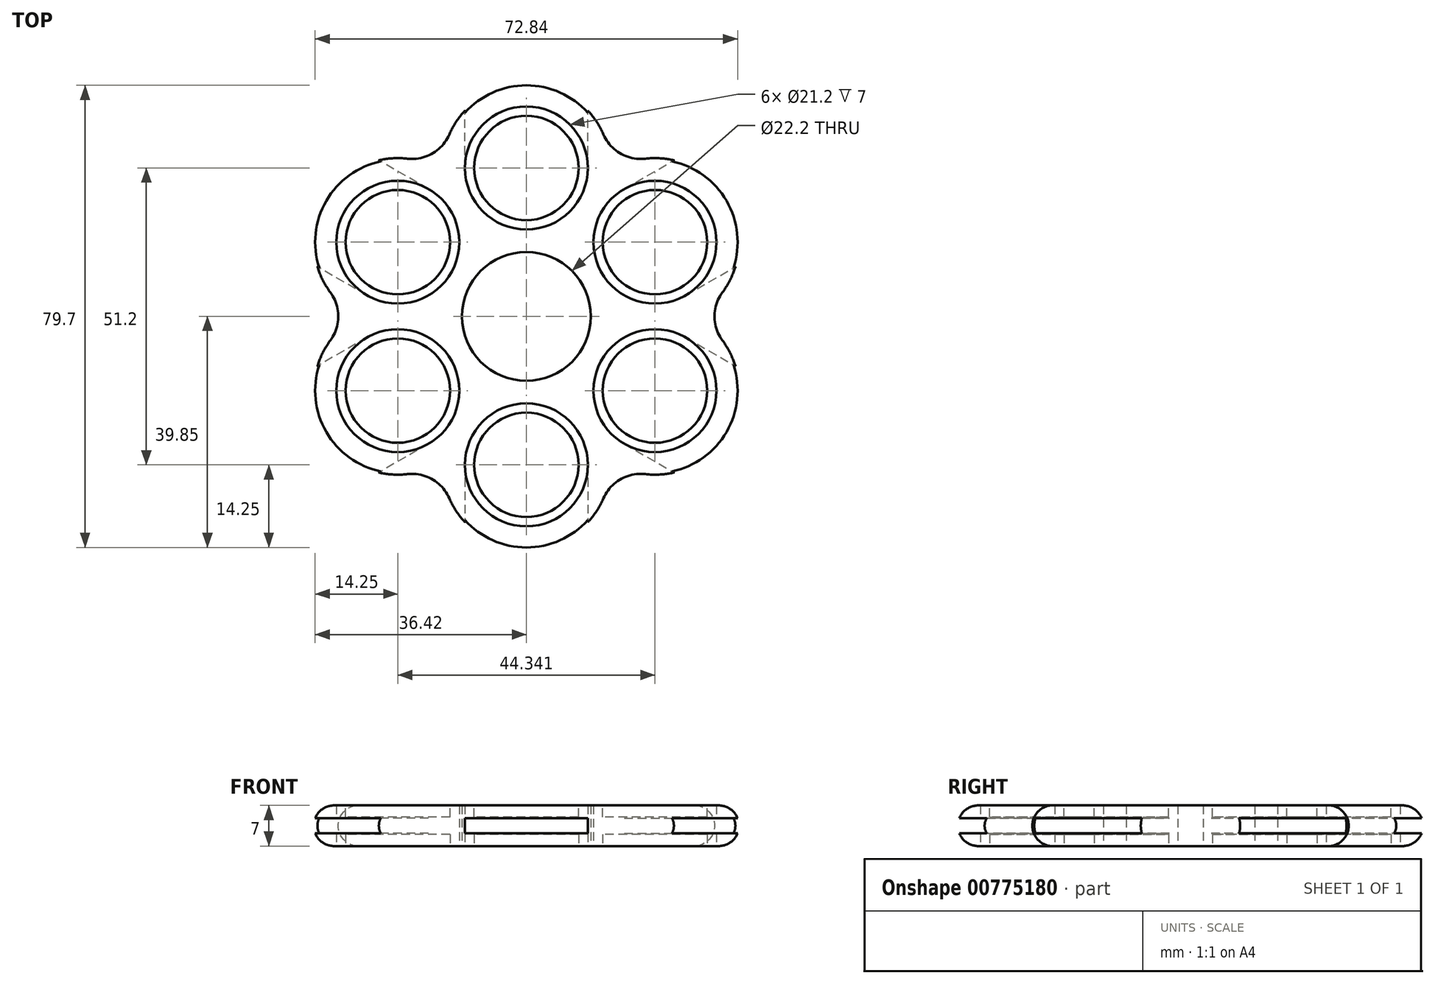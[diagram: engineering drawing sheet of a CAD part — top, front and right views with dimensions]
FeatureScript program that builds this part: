
annotation { "Feature Type Name" : "Feature", "Feature Type Description" : "" }
export const myFeature = defineFeature(function(context is Context, id is Id, definition is map)
    precondition{}
    {
        {
            var Q0;
            Q0=qCreatedBy(makeId("Top.planeOp"),FACE);
            var sketch = newSketch(context, id + "F0", { "sketchPlane" : qUnion([Q0])});
            skCircle(sketch, "E0", {"center": v(0, 0) * mm, "radius": 15 * mm});
            skCircle(sketch, "E1", {"center": v(0, 0) * mm, "radius": 11.1 * mm});
            skCircle(sketch, "E2", {"center": v(0, 25.6) * mm, "radius": 10.6 * mm});
            skCircle(sketch, "E3", {"center": v(0, 25.6) * mm, "radius": 14.5 * mm});
            skLineSegment(sketch, "E4", {"start": v(-10.6, 25.6) * mm, "end": v(-10.6, 40.6) * mm});
            skLineSegment(sketch, "E5.MirrorCS", {"start": v(10.6, 25.6) * mm, "end": v(10.6, 40.6) * mm});
            skLineSegment(sketch, "E6", {"start": v(-10.6, 40.6) * mm, "end": v(10.6, 40.6) * mm});
            skCircle(sketch, "E7.MirrorC", {"center": v(0, 25.6) * mm, "radius": 9 * mm});
            skLineSegment(sketch, "E8.1.0", {"start": v(-16.87, 21.98) * mm, "end": v(-29.86, 29.48) * mm});
            skCircle(sketch, "E8.1.1", {"center": v(-22.17, 12.8) * mm, "radius": 10.6 * mm});
            skCircle(sketch, "E8.1.2", {"center": v(-22.17, 12.8) * mm, "radius": 14.5 * mm});
            skCircle(sketch, "E8.1.3", {"center": v(-22.17, 12.8) * mm, "radius": 9 * mm});
            skLineSegment(sketch, "E8.1.4", {"start": v(-27.47, 3.62) * mm, "end": v(-40.46, 11.12) * mm});
            skLineSegment(sketch, "E8.2.0", {"start": v(-27.47, -3.62) * mm, "end": v(-40.46, -11.12) * mm});
            skCircle(sketch, "E8.2.1", {"center": v(-22.17, -12.8) * mm, "radius": 10.6 * mm});
            skCircle(sketch, "E8.2.2", {"center": v(-22.17, -12.8) * mm, "radius": 14.5 * mm});
            skCircle(sketch, "E8.2.3", {"center": v(-22.17, -12.8) * mm, "radius": 9 * mm});
            skLineSegment(sketch, "E8.2.4", {"start": v(-16.87, -21.98) * mm, "end": v(-29.86, -29.48) * mm});
            skLineSegment(sketch, "E8.3.0", {"start": v(-10.6, -25.6) * mm, "end": v(-10.6, -40.6) * mm});
            skCircle(sketch, "E8.3.1", {"center": v(0, -25.6) * mm, "radius": 10.6 * mm});
            skCircle(sketch, "E8.3.2", {"center": v(0, -25.6) * mm, "radius": 14.5 * mm});
            skCircle(sketch, "E8.3.3", {"center": v(0, -25.6) * mm, "radius": 9 * mm});
            skLineSegment(sketch, "E8.3.4", {"start": v(10.6, -25.6) * mm, "end": v(10.6, -40.6) * mm});
            skLineSegment(sketch, "E8.4.0", {"start": v(16.87, -21.98) * mm, "end": v(29.86, -29.48) * mm});
            skCircle(sketch, "E8.4.1", {"center": v(22.17, -12.8) * mm, "radius": 10.6 * mm});
            skCircle(sketch, "E8.4.2", {"center": v(22.17, -12.8) * mm, "radius": 14.5 * mm});
            skCircle(sketch, "E8.4.3", {"center": v(22.17, -12.8) * mm, "radius": 9 * mm});
            skLineSegment(sketch, "E8.4.4", {"start": v(27.47, -3.62) * mm, "end": v(40.46, -11.12) * mm});
            skLineSegment(sketch, "E8.5.0", {"start": v(27.47, 3.62) * mm, "end": v(40.46, 11.12) * mm});
            skCircle(sketch, "E8.5.1", {"center": v(22.17, 12.8) * mm, "radius": 10.6 * mm});
            skCircle(sketch, "E8.5.2", {"center": v(22.17, 12.8) * mm, "radius": 14.5 * mm});
            skCircle(sketch, "E8.5.3", {"center": v(22.17, 12.8) * mm, "radius": 9 * mm});
            skLineSegment(sketch, "E8.5.4", {"start": v(16.87, 21.98) * mm, "end": v(29.86, 29.48) * mm});
            skSolve(sketch);
        }
        {
            var Q0;
            {var subQ3=sQuery(id+"F0.wireOp",EDGE,"E0");var subQ5=sQuery(id+"F0.wireOp",EDGE,"E8.1.2");var subQ10=makeQuery(id+"F0.imprint","INTERSECT",VERTEX,{"disambiguationData":[OD(0.0)],"derivedFrom":[subQ3,subQ5]});Q0=makeQuery(id+"F0.imprint","IMPRINT",FACE,{"disambiguationData":[TD([[makeQuery(id+"F0.imprint","IMPRINT",EDGE,{"disambiguationData":[TD([[subQ10,-1.0]])],"derivedFrom":subQ3}),-1.0]])]});}
            var Q1;
            {var subQ0=sQuery(id+"F0.wireOp",EDGE,"E8.1.2");var subQ1=sQuery(id+"F0.wireOp",EDGE,"E3");var subQ2=makeQuery(id+"F0.imprint","INTERSECT",VERTEX,{"disambiguationData":[OD(0.0)],"derivedFrom":[subQ1,subQ0]});Q1=makeQuery(id+"F0.imprint","IMPRINT",FACE,{"disambiguationData":[TD([[makeQuery(id+"F0.imprint","IMPRINT",EDGE,{"disambiguationData":[TD([[subQ2,-1.0]])],"derivedFrom":subQ1}),1.0]])]});}
            var Q2;
            {var subQ5=sQuery(id+"F0.wireOp",EDGE,"E0");var subQ8=sQuery(id+"F0.wireOp",EDGE,"E2");var subQ10=makeQuery(id+"F0.imprint","INTERSECT",VERTEX,{"derivedFrom":[subQ5,subQ8]});Q2=makeQuery(id+"F0.imprint","IMPRINT",FACE,{"disambiguationData":[TD([[makeQuery(id+"F0.imprint","IMPRINT",EDGE,{"disambiguationData":[TD([[subQ10,-1.0]])],"derivedFrom":subQ5}),-1.0]])]});}
            var Q3;
            {var subQ1=sQuery(id+"F0.wireOp",EDGE,"E3");var subQ7=sQuery(id+"F0.wireOp",EDGE,"E0");var subQ9=makeQuery(id+"F0.imprint","INTERSECT",VERTEX,{"disambiguationData":[OD(0.0)],"derivedFrom":[subQ7,subQ1]});Q3=makeQuery(id+"F0.imprint","IMPRINT",FACE,{"disambiguationData":[TD([[makeQuery(id+"F0.imprint","IMPRINT",EDGE,{"disambiguationData":[TD([[subQ9,-1.0]])],"derivedFrom":subQ7}),-1.0]])]});}
            var Q4;
            {var subQ0=sQuery(id+"F0.wireOp",EDGE,"E8.5.2");var subQ1=sQuery(id+"F0.wireOp",EDGE,"E3");var subQ2=makeQuery(id+"F0.imprint","INTERSECT",VERTEX,{"disambiguationData":[OD(0.0)],"derivedFrom":[subQ1,subQ0]});Q4=makeQuery(id+"F0.imprint","IMPRINT",FACE,{"disambiguationData":[TD([[makeQuery(id+"F0.imprint","IMPRINT",EDGE,{"disambiguationData":[TD([[subQ2,1.0]])],"derivedFrom":subQ1}),1.0]])]});}
            var Q5;
            {var subQ1=sQuery(id+"F0.wireOp",EDGE,"E0");var subQ6=sQuery(id+"F0.wireOp",EDGE,"E8.1.1");var subQ8=makeQuery(id+"F0.imprint","INTERSECT",VERTEX,{"derivedFrom":[subQ1,subQ6]});Q5=makeQuery(id+"F0.imprint","IMPRINT",FACE,{"disambiguationData":[TD([[makeQuery(id+"F0.imprint","IMPRINT",EDGE,{"disambiguationData":[TD([[subQ8,-1.0]])],"derivedFrom":subQ1}),-1.0]])]});}
            var Q6;
            {var subQ0=sQuery(id+"F0.wireOp",EDGE,"E8.2.2");var subQ1=sQuery(id+"F0.wireOp",EDGE,"E8.1.2");var subQ2=makeQuery(id+"F0.imprint","INTERSECT",VERTEX,{"disambiguationData":[OD(0.0)],"derivedFrom":[subQ1,subQ0]});Q6=makeQuery(id+"F0.imprint","IMPRINT",FACE,{"disambiguationData":[TD([[makeQuery(id+"F0.imprint","IMPRINT",EDGE,{"disambiguationData":[TD([[subQ2,-1.0]])],"derivedFrom":subQ1}),1.0]])]});}
            var Q7;
            {var subQ5=sQuery(id+"F0.wireOp",EDGE,"E0");var subQ8=sQuery(id+"F0.wireOp",EDGE,"E8.2.1");var subQ10=makeQuery(id+"F0.imprint","INTERSECT",VERTEX,{"derivedFrom":[subQ5,subQ8]});Q7=makeQuery(id+"F0.imprint","IMPRINT",FACE,{"disambiguationData":[TD([[makeQuery(id+"F0.imprint","IMPRINT",EDGE,{"disambiguationData":[TD([[subQ10,-1.0]])],"derivedFrom":subQ5}),-1.0]])]});}
            var Q8;
            {var subQ0=sQuery(id+"F0.wireOp",EDGE,"E8.3.2");var subQ1=sQuery(id+"F0.wireOp",EDGE,"E8.2.2");var subQ2=makeQuery(id+"F0.imprint","INTERSECT",VERTEX,{"disambiguationData":[OD(0.0)],"derivedFrom":[subQ1,subQ0]});Q8=makeQuery(id+"F0.imprint","IMPRINT",FACE,{"disambiguationData":[TD([[makeQuery(id+"F0.imprint","IMPRINT",EDGE,{"disambiguationData":[TD([[subQ2,-1.0]])],"derivedFrom":subQ1}),1.0]])]});}
            var Q9;
            {var subQ3=sQuery(id+"F0.wireOp",EDGE,"E0");var subQ5=sQuery(id+"F0.wireOp",EDGE,"E8.3.2");var subQ10=makeQuery(id+"F0.imprint","INTERSECT",VERTEX,{"disambiguationData":[OD(0.0)],"derivedFrom":[subQ3,subQ5]});Q9=makeQuery(id+"F0.imprint","IMPRINT",FACE,{"disambiguationData":[TD([[makeQuery(id+"F0.imprint","IMPRINT",EDGE,{"disambiguationData":[TD([[subQ10,-1.0]])],"derivedFrom":subQ3}),-1.0]])]});}
            var Q10;
            {var subQ5=sQuery(id+"F0.wireOp",EDGE,"E0");var subQ8=sQuery(id+"F0.wireOp",EDGE,"E8.3.1");var subQ9=makeQuery(id+"F0.imprint","INTERSECT",VERTEX,{"derivedFrom":[subQ5,subQ8]});Q10=makeQuery(id+"F0.imprint","IMPRINT",FACE,{"disambiguationData":[TD([[makeQuery(id+"F0.imprint","IMPRINT",EDGE,{"disambiguationData":[TD([[subQ9,-1.0]])],"derivedFrom":subQ5}),-1.0]])]});}
            var Q11;
            {var subQ0=sQuery(id+"F0.wireOp",EDGE,"E8.4.2");var subQ1=sQuery(id+"F0.wireOp",EDGE,"E8.3.2");var subQ2=makeQuery(id+"F0.imprint","INTERSECT",VERTEX,{"disambiguationData":[OD(0.0)],"derivedFrom":[subQ1,subQ0]});Q11=makeQuery(id+"F0.imprint","IMPRINT",FACE,{"disambiguationData":[TD([[makeQuery(id+"F0.imprint","IMPRINT",EDGE,{"disambiguationData":[TD([[subQ2,-1.0]])],"derivedFrom":subQ1}),1.0]])]});}
            var Q12;
            {var subQ3=sQuery(id+"F0.wireOp",EDGE,"E8.4.2");var subQ8=sQuery(id+"F0.wireOp",EDGE,"E0");var subQ10=makeQuery(id+"F0.imprint","INTERSECT",VERTEX,{"disambiguationData":[OD(0.0)],"derivedFrom":[subQ8,subQ3]});Q12=makeQuery(id+"F0.imprint","IMPRINT",FACE,{"disambiguationData":[TD([[makeQuery(id+"F0.imprint","IMPRINT",EDGE,{"disambiguationData":[TD([[subQ10,-1.0]])],"derivedFrom":subQ8}),-1.0]])]});}
            var Q13;
            {var subQ5=sQuery(id+"F0.wireOp",EDGE,"E0");var subQ8=sQuery(id+"F0.wireOp",EDGE,"E8.4.1");var subQ10=makeQuery(id+"F0.imprint","INTERSECT",VERTEX,{"derivedFrom":[subQ5,subQ8]});Q13=makeQuery(id+"F0.imprint","IMPRINT",FACE,{"disambiguationData":[TD([[makeQuery(id+"F0.imprint","IMPRINT",EDGE,{"disambiguationData":[TD([[subQ10,-1.0]])],"derivedFrom":subQ5}),-1.0]])]});}
            var Q14;
            {var subQ0=sQuery(id+"F0.wireOp",EDGE,"E8.5.2");var subQ1=sQuery(id+"F0.wireOp",EDGE,"E8.4.2");var subQ2=makeQuery(id+"F0.imprint","INTERSECT",VERTEX,{"disambiguationData":[OD(0.0)],"derivedFrom":[subQ1,subQ0]});Q14=makeQuery(id+"F0.imprint","IMPRINT",FACE,{"disambiguationData":[TD([[makeQuery(id+"F0.imprint","IMPRINT",EDGE,{"disambiguationData":[TD([[subQ2,-1.0]])],"derivedFrom":subQ1}),1.0]])]});}
            var Q15;
            {var subQ0=sQuery(id+"F0.wireOp",EDGE,"E8.5.1");var subQ8=sQuery(id+"F0.wireOp",EDGE,"E0");var subQ9=makeQuery(id+"F0.imprint","INTERSECT",VERTEX,{"derivedFrom":[subQ8,subQ0]});Q15=makeQuery(id+"F0.imprint","IMPRINT",FACE,{"disambiguationData":[TD([[makeQuery(id+"F0.imprint","IMPRINT",EDGE,{"disambiguationData":[TD([[subQ9,1.0]])],"derivedFrom":subQ8}),-1.0]])]});}
            var Q16;
            {var subQ5=sQuery(id+"F0.wireOp",EDGE,"E8.5.1");var subQ7=sQuery(id+"F0.wireOp",EDGE,"E0");var subQ8=makeQuery(id+"F0.imprint","INTERSECT",VERTEX,{"derivedFrom":[subQ7,subQ5]});Q16=makeQuery(id+"F0.imprint","IMPRINT",FACE,{"disambiguationData":[TD([[makeQuery(id+"F0.imprint","IMPRINT",EDGE,{"disambiguationData":[TD([[subQ8,-1.0]])],"derivedFrom":subQ7}),-1.0]])]});}
            var Q17;
            {var subQ3=sQuery(id+"F0.wireOp",EDGE,"E0");var subQ5=sQuery(id+"F0.wireOp",EDGE,"E8.2.2");var subQ10=makeQuery(id+"F0.imprint","INTERSECT",VERTEX,{"disambiguationData":[OD(0.0)],"derivedFrom":[subQ3,subQ5]});Q17=makeQuery(id+"F0.imprint","IMPRINT",FACE,{"disambiguationData":[TD([[makeQuery(id+"F0.imprint","IMPRINT",EDGE,{"disambiguationData":[TD([[subQ10,-1.0]])],"derivedFrom":subQ3}),-1.0]])]});}
            var Q18;
            {var subQ0=sQuery(id+"F0.wireOp",EDGE,"E8.2.2");var subQ1=sQuery(id+"F0.wireOp",EDGE,"E0");var subQ2=makeQuery(id+"F0.imprint","INTERSECT",VERTEX,{"disambiguationData":[OD(0.0)],"derivedFrom":[subQ1,subQ0]});Q18=makeQuery(id+"F0.imprint","IMPRINT",FACE,{"disambiguationData":[TD([[makeQuery(id+"F0.imprint","IMPRINT",EDGE,{"disambiguationData":[TD([[subQ2,-1.0]])],"derivedFrom":subQ1}),1.0]])]});}
            var Q19;
            {var subQ0=sQuery(id+"F0.wireOp",EDGE,"E8.1.2");var subQ1=sQuery(id+"F0.wireOp",EDGE,"E0");var subQ2=makeQuery(id+"F0.imprint","INTERSECT",VERTEX,{"disambiguationData":[OD(0.0)],"derivedFrom":[subQ1,subQ0]});Q19=makeQuery(id+"F0.imprint","IMPRINT",FACE,{"disambiguationData":[TD([[makeQuery(id+"F0.imprint","IMPRINT",EDGE,{"disambiguationData":[TD([[subQ2,-1.0]])],"derivedFrom":subQ1}),1.0]])]});}
            var Q20;
            {var subQ0=sQuery(id+"F0.wireOp",EDGE,"E3");var subQ1=sQuery(id+"F0.wireOp",EDGE,"E0");var subQ2=makeQuery(id+"F0.imprint","INTERSECT",VERTEX,{"disambiguationData":[OD(0.0)],"derivedFrom":[subQ1,subQ0]});Q20=makeQuery(id+"F0.imprint","IMPRINT",FACE,{"disambiguationData":[TD([[makeQuery(id+"F0.imprint","IMPRINT",EDGE,{"disambiguationData":[TD([[subQ2,-1.0]])],"derivedFrom":subQ1}),1.0]])]});}
            var Q21;
            {var subQ0=sQuery(id+"F0.wireOp",EDGE,"E0");var subQ1=makeQuery(id+"F0.imprint","INTERSECT",VERTEX,{"derivedFrom":[subQ0,sQuery(id+"F0.wireOp",EDGE,"E8.5.1")]});Q21=makeQuery(id+"F0.imprint","IMPRINT",FACE,{"disambiguationData":[TD([[makeQuery(id+"F0.imprint","IMPRINT",EDGE,{"disambiguationData":[TD([[subQ1,1.0]])],"derivedFrom":subQ0}),1.0]])]});}
            var Q22;
            {var subQ0=sQuery(id+"F0.wireOp",EDGE,"E8.4.2");var subQ1=sQuery(id+"F0.wireOp",EDGE,"E0");var subQ2=makeQuery(id+"F0.imprint","INTERSECT",VERTEX,{"disambiguationData":[OD(0.0)],"derivedFrom":[subQ1,subQ0]});Q22=makeQuery(id+"F0.imprint","IMPRINT",FACE,{"disambiguationData":[TD([[makeQuery(id+"F0.imprint","IMPRINT",EDGE,{"disambiguationData":[TD([[subQ2,-1.0]])],"derivedFrom":subQ1}),1.0]])]});}
            var Q23;
            {var subQ0=sQuery(id+"F0.wireOp",EDGE,"E8.3.2");var subQ1=sQuery(id+"F0.wireOp",EDGE,"E0");var subQ2=makeQuery(id+"F0.imprint","INTERSECT",VERTEX,{"disambiguationData":[OD(0.0)],"derivedFrom":[subQ1,subQ0]});Q23=makeQuery(id+"F0.imprint","IMPRINT",FACE,{"disambiguationData":[TD([[makeQuery(id+"F0.imprint","IMPRINT",EDGE,{"disambiguationData":[TD([[subQ2,-1.0]])],"derivedFrom":subQ1}),1.0]])]});}
            var Q24;
            {var subQ0=sQuery(id+"F0.wireOp",EDGE,"E8.2.2");var subQ1=sQuery(id+"F0.wireOp",EDGE,"E0");var subQ2=makeQuery(id+"F0.imprint","INTERSECT",VERTEX,{"disambiguationData":[OD(1.0)],"derivedFrom":[subQ1,subQ0]});Q24=makeQuery(id+"F0.imprint","IMPRINT",FACE,{"disambiguationData":[TD([[makeQuery(id+"F0.imprint","IMPRINT",EDGE,{"disambiguationData":[TD([[subQ2,-1.0]])],"derivedFrom":subQ1}),1.0]])]});}
            var Q25;
            {var subQ0=sQuery(id+"F0.wireOp",EDGE,"E8.1.2");var subQ1=sQuery(id+"F0.wireOp",EDGE,"E0");var subQ2=makeQuery(id+"F0.imprint","INTERSECT",VERTEX,{"disambiguationData":[OD(1.0)],"derivedFrom":[subQ1,subQ0]});Q25=makeQuery(id+"F0.imprint","IMPRINT",FACE,{"disambiguationData":[TD([[makeQuery(id+"F0.imprint","IMPRINT",EDGE,{"disambiguationData":[TD([[subQ2,-1.0]])],"derivedFrom":subQ1}),1.0]])]});}
            var Q26;
            {var subQ0=sQuery(id+"F0.wireOp",EDGE,"E3");var subQ1=sQuery(id+"F0.wireOp",EDGE,"E0");var subQ2=makeQuery(id+"F0.imprint","INTERSECT",VERTEX,{"disambiguationData":[OD(1.0)],"derivedFrom":[subQ1,subQ0]});Q26=makeQuery(id+"F0.imprint","IMPRINT",FACE,{"disambiguationData":[TD([[makeQuery(id+"F0.imprint","IMPRINT",EDGE,{"disambiguationData":[TD([[subQ2,-1.0]])],"derivedFrom":subQ1}),1.0]])]});}
            var Q27;
            {var subQ0=sQuery(id+"F0.wireOp",EDGE,"E8.5.2");var subQ1=sQuery(id+"F0.wireOp",EDGE,"E0");var subQ2=makeQuery(id+"F0.imprint","INTERSECT",VERTEX,{"disambiguationData":[OD(1.0)],"derivedFrom":[subQ1,subQ0]});Q27=makeQuery(id+"F0.imprint","IMPRINT",FACE,{"disambiguationData":[TD([[makeQuery(id+"F0.imprint","IMPRINT",EDGE,{"disambiguationData":[TD([[subQ2,-1.0]])],"derivedFrom":subQ1}),1.0]])]});}
            var Q28;
            {var subQ0=sQuery(id+"F0.wireOp",EDGE,"E8.5.2");var subQ1=sQuery(id+"F0.wireOp",EDGE,"E0");var subQ2=makeQuery(id+"F0.imprint","INTERSECT",VERTEX,{"disambiguationData":[OD(0.0)],"derivedFrom":[subQ1,subQ0]});Q28=makeQuery(id+"F0.imprint","IMPRINT",FACE,{"disambiguationData":[TD([[makeQuery(id+"F0.imprint","IMPRINT",EDGE,{"disambiguationData":[TD([[subQ2,1.0]])],"derivedFrom":subQ1}),1.0]])]});}
            var Q29;
            {var subQ0=sQuery(id+"F0.wireOp",EDGE,"E8.3.2");var subQ1=sQuery(id+"F0.wireOp",EDGE,"E0");var subQ2=makeQuery(id+"F0.imprint","INTERSECT",VERTEX,{"disambiguationData":[OD(1.0)],"derivedFrom":[subQ1,subQ0]});Q29=makeQuery(id+"F0.imprint","IMPRINT",FACE,{"disambiguationData":[TD([[makeQuery(id+"F0.imprint","IMPRINT",EDGE,{"disambiguationData":[TD([[subQ2,-1.0]])],"derivedFrom":subQ1}),1.0]])]});}
            var Q30;
            {var subQ0=sQuery(id+"F0.wireOp",EDGE,"E8.1.2");var subQ1=sQuery(id+"F0.wireOp",EDGE,"E0");var subQ2=makeQuery(id+"F0.imprint","INTERSECT",VERTEX,{"disambiguationData":[OD(1.0)],"derivedFrom":[subQ1,subQ0]});Q30=makeQuery(id+"F0.imprint","IMPRINT",FACE,{"disambiguationData":[TD([[makeQuery(id+"F0.imprint","IMPRINT",EDGE,{"disambiguationData":[TD([[subQ2,-1.0]])],"derivedFrom":subQ1}),-1.0]])]});}
            var Q31;
            {var subQ0=sQuery(id+"F0.wireOp",EDGE,"E3");var subQ1=sQuery(id+"F0.wireOp",EDGE,"E0");var subQ2=makeQuery(id+"F0.imprint","INTERSECT",VERTEX,{"disambiguationData":[OD(1.0)],"derivedFrom":[subQ1,subQ0]});Q31=makeQuery(id+"F0.imprint","IMPRINT",FACE,{"disambiguationData":[TD([[makeQuery(id+"F0.imprint","IMPRINT",EDGE,{"disambiguationData":[TD([[subQ2,-1.0]])],"derivedFrom":subQ1}),-1.0]])]});}
            var Q32;
            {var subQ0=sQuery(id+"F0.wireOp",EDGE,"E8.5.2");var subQ1=sQuery(id+"F0.wireOp",EDGE,"E0");var subQ2=makeQuery(id+"F0.imprint","INTERSECT",VERTEX,{"disambiguationData":[OD(1.0)],"derivedFrom":[subQ1,subQ0]});Q32=makeQuery(id+"F0.imprint","IMPRINT",FACE,{"disambiguationData":[TD([[makeQuery(id+"F0.imprint","IMPRINT",EDGE,{"disambiguationData":[TD([[subQ2,-1.0]])],"derivedFrom":subQ1}),-1.0]])]});}
            var Q33;
            {var subQ0=sQuery(id+"F0.wireOp",EDGE,"E8.5.2");var subQ1=sQuery(id+"F0.wireOp",EDGE,"E0");var subQ2=makeQuery(id+"F0.imprint","INTERSECT",VERTEX,{"disambiguationData":[OD(0.0)],"derivedFrom":[subQ1,subQ0]});Q33=makeQuery(id+"F0.imprint","IMPRINT",FACE,{"disambiguationData":[TD([[makeQuery(id+"F0.imprint","IMPRINT",EDGE,{"disambiguationData":[TD([[subQ2,1.0]])],"derivedFrom":subQ1}),-1.0]])]});}
            var Q34;
            {var subQ0=sQuery(id+"F0.wireOp",EDGE,"E8.3.2");var subQ1=sQuery(id+"F0.wireOp",EDGE,"E0");var subQ2=makeQuery(id+"F0.imprint","INTERSECT",VERTEX,{"disambiguationData":[OD(1.0)],"derivedFrom":[subQ1,subQ0]});Q34=makeQuery(id+"F0.imprint","IMPRINT",FACE,{"disambiguationData":[TD([[makeQuery(id+"F0.imprint","IMPRINT",EDGE,{"disambiguationData":[TD([[subQ2,-1.0]])],"derivedFrom":subQ1}),-1.0]])]});}
            var Q35;
            {var subQ0=sQuery(id+"F0.wireOp",EDGE,"E8.2.2");var subQ1=sQuery(id+"F0.wireOp",EDGE,"E0");var subQ2=makeQuery(id+"F0.imprint","INTERSECT",VERTEX,{"disambiguationData":[OD(1.0)],"derivedFrom":[subQ1,subQ0]});Q35=makeQuery(id+"F0.imprint","IMPRINT",FACE,{"disambiguationData":[TD([[makeQuery(id+"F0.imprint","IMPRINT",EDGE,{"disambiguationData":[TD([[subQ2,-1.0]])],"derivedFrom":subQ1}),-1.0]])]});}
            extrude(context, id + "F1", {"entities" : qUnion([Q0, Q1, Q2, Q3, Q4, Q5, Q6, Q7, Q8, Q9, Q10, Q11, Q12, Q13, Q14, Q15, Q16, Q17, Q18, Q19, Q20, Q21, Q22, Q23, Q24, Q25, Q26, Q27, Q28, Q29, Q30, Q31, Q32, Q33, Q34, Q35]), "depth" : 7 * mm, "offsetDistance" : 25 * mm});
        }
        {
            var Q0;
            {var subQ0=sQuery(id+"F0.wireOp",EDGE,"E8.1.1");var subQ1=sQuery(id+"F0.wireOp",EDGE,"E8.1.0");var subQ2=makeQuery(id+"F0.imprint","INTERSECT",VERTEX,{"derivedFrom":[subQ1,subQ0]});Q0=makeQuery(id+"F0.imprint","IMPRINT",FACE,{"disambiguationData":[TD([[makeQuery(id+"F0.imprint","IMPRINT",EDGE,{"disambiguationData":[TD([[subQ2,-1.0]])],"derivedFrom":subQ1}),1.0]])]});}
            var Q1;
            {var subQ0=sQuery(id+"F0.wireOp",EDGE,"E4");var subQ1=sQuery(id+"F0.wireOp",EDGE,"E2");var subQ2=makeQuery(id+"F0.imprint","INTERSECT",VERTEX,{"derivedFrom":[subQ1,subQ0]});Q1=makeQuery(id+"F0.imprint","IMPRINT",FACE,{"disambiguationData":[TD([[makeQuery(id+"F0.imprint","IMPRINT",EDGE,{"disambiguationData":[TD([[subQ2,1.0]])],"derivedFrom":subQ1}),-1.0]])]});}
            var Q2;
            {var subQ0=sQuery(id+"F0.wireOp",EDGE,"E8.5.1");var subQ1=sQuery(id+"F0.wireOp",EDGE,"E8.5.0");var subQ2=makeQuery(id+"F0.imprint","INTERSECT",VERTEX,{"derivedFrom":[subQ1,subQ0]});Q2=makeQuery(id+"F0.imprint","IMPRINT",FACE,{"disambiguationData":[TD([[makeQuery(id+"F0.imprint","IMPRINT",EDGE,{"disambiguationData":[TD([[subQ2,-1.0]])],"derivedFrom":subQ1}),1.0]])]});}
            var Q3;
            {var subQ0=sQuery(id+"F0.wireOp",EDGE,"E8.4.1");var subQ1=sQuery(id+"F0.wireOp",EDGE,"E8.4.0");var subQ2=makeQuery(id+"F0.imprint","INTERSECT",VERTEX,{"derivedFrom":[subQ1,subQ0]});Q3=makeQuery(id+"F0.imprint","IMPRINT",FACE,{"disambiguationData":[TD([[makeQuery(id+"F0.imprint","IMPRINT",EDGE,{"disambiguationData":[TD([[subQ2,-1.0]])],"derivedFrom":subQ1}),1.0]])]});}
            var Q4;
            {var subQ0=sQuery(id+"F0.wireOp",EDGE,"E8.3.1");var subQ1=sQuery(id+"F0.wireOp",EDGE,"E8.3.0");var subQ2=makeQuery(id+"F0.imprint","INTERSECT",VERTEX,{"derivedFrom":[subQ1,subQ0]});Q4=makeQuery(id+"F0.imprint","IMPRINT",FACE,{"disambiguationData":[TD([[makeQuery(id+"F0.imprint","IMPRINT",EDGE,{"disambiguationData":[TD([[subQ2,-1.0]])],"derivedFrom":subQ1}),1.0]])]});}
            var Q5;
            {var subQ0=sQuery(id+"F0.wireOp",EDGE,"E8.2.1");var subQ1=sQuery(id+"F0.wireOp",EDGE,"E8.2.0");var subQ2=makeQuery(id+"F0.imprint","INTERSECT",VERTEX,{"derivedFrom":[subQ1,subQ0]});Q5=makeQuery(id+"F0.imprint","IMPRINT",FACE,{"disambiguationData":[TD([[makeQuery(id+"F0.imprint","IMPRINT",EDGE,{"disambiguationData":[TD([[subQ2,-1.0]])],"derivedFrom":subQ1}),1.0]])]});}
            extrude(context, id + "F2", {"entities" : qUnion([Q0, Q1, Q2, Q3, Q4, Q5]), "operationType" : NewBodyOperationType.ADD, "depth" : 2.2 * mm, "offsetDistance" : 25 * mm});
        }
        {
            var Q0;
            Q0=makeQuery(id+"F0.imprint","IMPRINT",FACE,{"disambiguationData":[TD([[makeQuery(id+"F0.imprint","IMPRINT",EDGE,{"derivedFrom":sQuery(id+"F0.wireOp",EDGE,"E8.2.3")}),1.0]])]});
            var Q1;
            Q1=makeQuery(id+"F0.imprint","IMPRINT",FACE,{"disambiguationData":[TD([[makeQuery(id+"F0.imprint","IMPRINT",EDGE,{"derivedFrom":sQuery(id+"F0.wireOp",EDGE,"E8.3.3")}),1.0]])]});
            var Q2;
            Q2=makeQuery(id+"F0.imprint","IMPRINT",FACE,{"disambiguationData":[TD([[makeQuery(id+"F0.imprint","IMPRINT",EDGE,{"derivedFrom":sQuery(id+"F0.wireOp",EDGE,"E8.4.3")}),1.0]])]});
            var Q3;
            Q3=makeQuery(id+"F0.imprint","IMPRINT",FACE,{"disambiguationData":[TD([[makeQuery(id+"F0.imprint","IMPRINT",EDGE,{"derivedFrom":sQuery(id+"F0.wireOp",EDGE,"E8.5.3")}),1.0]])]});
            var Q4;
            Q4=makeQuery(id+"F0.imprint","IMPRINT",FACE,{"disambiguationData":[TD([[makeQuery(id+"F0.imprint","IMPRINT",EDGE,{"derivedFrom":sQuery(id+"F0.wireOp",EDGE,"E7.MirrorC")}),1.0]])]});
            var Q5;
            Q5=makeQuery(id+"F0.imprint","IMPRINT",FACE,{"disambiguationData":[TD([[makeQuery(id+"F0.imprint","IMPRINT",EDGE,{"derivedFrom":sQuery(id+"F0.wireOp",EDGE,"E8.1.3")}),1.0]])]});
            extrude(context, id + "F3", {"entities" : qUnion([Q0, Q1, Q2, Q3, Q4, Q5]), "operationType" : NewBodyOperationType.ADD, "depth" : 2 * mm, "offsetDistance" : 25 * mm});
        }
        {
            var Q0;
            Q0=makeQuery(id+"F1.opExtrude","CAP_FACE",FACE,{"disambiguationData":[OSD([sQuery(id+"F0.wireOp",EDGE,"E0"),sQuery(id+"F0.wireOp",EDGE,"E1"),sQuery(id+"F0.wireOp",EDGE,"E2"),sQuery(id+"F0.wireOp",EDGE,"E3"),sQuery(id+"F0.wireOp",EDGE,"E4"),sQuery(id+"F0.wireOp",EDGE,"E5.MirrorCS"),sQuery(id+"F0.wireOp",EDGE,"E8.1.0"),sQuery(id+"F0.wireOp",EDGE,"E8.1.1"),sQuery(id+"F0.wireOp",EDGE,"E8.1.2"),sQuery(id+"F0.wireOp",EDGE,"E8.1.4"),sQuery(id+"F0.wireOp",EDGE,"E8.2.0"),sQuery(id+"F0.wireOp",EDGE,"E8.2.1"),sQuery(id+"F0.wireOp",EDGE,"E8.2.2"),sQuery(id+"F0.wireOp",EDGE,"E8.2.4"),sQuery(id+"F0.wireOp",EDGE,"E8.3.0"),sQuery(id+"F0.wireOp",EDGE,"E8.3.1"),sQuery(id+"F0.wireOp",EDGE,"E8.3.2"),sQuery(id+"F0.wireOp",EDGE,"E8.3.4"),sQuery(id+"F0.wireOp",EDGE,"E8.4.0"),sQuery(id+"F0.wireOp",EDGE,"E8.4.1"),sQuery(id+"F0.wireOp",EDGE,"E8.4.2"),sQuery(id+"F0.wireOp",EDGE,"E8.4.4"),sQuery(id+"F0.wireOp",EDGE,"E8.5.0"),sQuery(id+"F0.wireOp",EDGE,"E8.5.1"),sQuery(id+"F0.wireOp",EDGE,"E8.5.2"),sQuery(id+"F0.wireOp",EDGE,"E8.5.4")])],"isStart":false});
            var sketch = newSketch(context, id + "F4", { "sketchPlane" : qUnion([Q0])});
            skCircle(sketch, "E9", {"center": v(0, 0) * mm, "radius": 15 * mm});
            skCircle(sketch, "E10", {"center": v(0, 0) * mm, "radius": 11.1 * mm});
            skCircle(sketch, "E11", {"center": v(0, 25.6) * mm, "radius": 10.6 * mm});
            skCircle(sketch, "E12", {"center": v(0, 25.6) * mm, "radius": 14.5 * mm});
            skLineSegment(sketch, "E13", {"start": v(-10.6, 25.6) * mm, "end": v(-10.6, 40.6) * mm});
            skLineSegment(sketch, "E14.MirrorCS", {"start": v(10.6, 25.6) * mm, "end": v(10.6, 41.1) * mm});
            skLineSegment(sketch, "E15", {"start": v(-10.6, 40.6) * mm, "end": v(10.6, 41.1) * mm});
            skCircle(sketch, "E16.MirrorC", {"center": v(0, 25.6) * mm, "radius": 9 * mm});
            skLineSegment(sketch, "E17.1.0", {"start": v(-16.87, 21.98) * mm, "end": v(-30.3, 29.73) * mm});
            skCircle(sketch, "E17.1.1", {"center": v(-22.17, 12.8) * mm, "radius": 10.6 * mm});
            skCircle(sketch, "E17.1.2", {"center": v(-22.17, 12.8) * mm, "radius": 14.5 * mm});
            skCircle(sketch, "E17.1.3", {"center": v(-22.17, 12.8) * mm, "radius": 9 * mm});
            skLineSegment(sketch, "E17.1.4", {"start": v(-27.47, 3.62) * mm, "end": v(-40.46, 11.12) * mm});
            skLineSegment(sketch, "E17.2.0", {"start": v(-27.47, -3.62) * mm, "end": v(-40.9, -11.37) * mm});
            skCircle(sketch, "E17.2.1", {"center": v(-22.17, -12.8) * mm, "radius": 10.6 * mm});
            skCircle(sketch, "E17.2.2", {"center": v(-22.17, -12.8) * mm, "radius": 14.5 * mm});
            skCircle(sketch, "E17.2.3", {"center": v(-22.17, -12.8) * mm, "radius": 9 * mm});
            skLineSegment(sketch, "E17.2.4", {"start": v(-16.87, -21.98) * mm, "end": v(-29.86, -29.48) * mm});
            skLineSegment(sketch, "E17.3.0", {"start": v(-10.6, -25.6) * mm, "end": v(-10.6, -41.1) * mm});
            skCircle(sketch, "E17.3.1", {"center": v(0, -25.6) * mm, "radius": 10.6 * mm});
            skCircle(sketch, "E17.3.2", {"center": v(0, -25.6) * mm, "radius": 14.5 * mm});
            skCircle(sketch, "E17.3.3", {"center": v(0, -25.6) * mm, "radius": 9 * mm});
            skLineSegment(sketch, "E17.3.4", {"start": v(10.6, -25.6) * mm, "end": v(10.6, -40.6) * mm});
            skLineSegment(sketch, "E17.4.0", {"start": v(16.87, -21.98) * mm, "end": v(30.3, -29.73) * mm});
            skCircle(sketch, "E17.4.1", {"center": v(22.17, -12.8) * mm, "radius": 10.6 * mm});
            skCircle(sketch, "E17.4.2", {"center": v(22.17, -12.8) * mm, "radius": 14.5 * mm});
            skCircle(sketch, "E17.4.3", {"center": v(22.17, -12.8) * mm, "radius": 9 * mm});
            skLineSegment(sketch, "E17.4.4", {"start": v(27.47, -3.62) * mm, "end": v(40.46, -11.12) * mm});
            skLineSegment(sketch, "E17.5.0", {"start": v(27.47, 3.62) * mm, "end": v(40.9, 11.37) * mm});
            skCircle(sketch, "E17.5.1", {"center": v(22.17, 12.8) * mm, "radius": 10.6 * mm});
            skCircle(sketch, "E17.5.2", {"center": v(22.17, 12.8) * mm, "radius": 14.5 * mm});
            skCircle(sketch, "E17.5.3", {"center": v(22.17, 12.8) * mm, "radius": 9 * mm});
            skLineSegment(sketch, "E17.5.4", {"start": v(16.87, 21.98) * mm, "end": v(29.86, 29.48) * mm});
            skSolve(sketch);
        }
        {
            var Q0;
            {var subQ0=sQuery(id+"F4.wireOp",EDGE,"E17.5.1");var subQ1=sQuery(id+"F4.wireOp",EDGE,"E17.5.0");var subQ2=makeQuery(id+"F4.imprint","INTERSECT",VERTEX,{"derivedFrom":[subQ1,subQ0]});Q0=makeQuery(id+"F4.imprint","IMPRINT",FACE,{"disambiguationData":[TD([[makeQuery(id+"F4.imprint","IMPRINT",EDGE,{"disambiguationData":[TD([[subQ2,-1.0]])],"derivedFrom":subQ1}),1.0]])]});}
            var Q1;
            {var subQ0=sQuery(id+"F4.wireOp",EDGE,"E17.4.1");var subQ1=sQuery(id+"F4.wireOp",EDGE,"E17.4.0");var subQ2=makeQuery(id+"F4.imprint","INTERSECT",VERTEX,{"derivedFrom":[subQ1,subQ0]});Q1=makeQuery(id+"F4.imprint","IMPRINT",FACE,{"disambiguationData":[TD([[makeQuery(id+"F4.imprint","IMPRINT",EDGE,{"disambiguationData":[TD([[subQ2,-1.0]])],"derivedFrom":subQ1}),1.0]])]});}
            var Q2;
            {var subQ0=sQuery(id+"F4.wireOp",EDGE,"E13");var subQ1=sQuery(id+"F4.wireOp",EDGE,"E11");var subQ2=makeQuery(id+"F4.imprint","INTERSECT",VERTEX,{"derivedFrom":[subQ1,subQ0]});Q2=makeQuery(id+"F4.imprint","IMPRINT",FACE,{"disambiguationData":[TD([[makeQuery(id+"F4.imprint","IMPRINT",EDGE,{"disambiguationData":[TD([[subQ2,1.0]])],"derivedFrom":subQ1}),-1.0]])]});}
            var Q3;
            {var subQ0=sQuery(id+"F4.wireOp",EDGE,"E17.1.1");var subQ1=sQuery(id+"F4.wireOp",EDGE,"E17.1.0");var subQ2=makeQuery(id+"F4.imprint","INTERSECT",VERTEX,{"derivedFrom":[subQ1,subQ0]});Q3=makeQuery(id+"F4.imprint","IMPRINT",FACE,{"disambiguationData":[TD([[makeQuery(id+"F4.imprint","IMPRINT",EDGE,{"disambiguationData":[TD([[subQ2,-1.0]])],"derivedFrom":subQ1}),1.0]])]});}
            var Q4;
            {var subQ0=sQuery(id+"F4.wireOp",EDGE,"E17.2.1");var subQ1=sQuery(id+"F4.wireOp",EDGE,"E17.2.0");var subQ2=makeQuery(id+"F4.imprint","INTERSECT",VERTEX,{"derivedFrom":[subQ1,subQ0]});Q4=makeQuery(id+"F4.imprint","IMPRINT",FACE,{"disambiguationData":[TD([[makeQuery(id+"F4.imprint","IMPRINT",EDGE,{"disambiguationData":[TD([[subQ2,-1.0]])],"derivedFrom":subQ1}),1.0]])]});}
            var Q5;
            {var subQ0=sQuery(id+"F4.wireOp",EDGE,"E17.3.1");var subQ1=sQuery(id+"F4.wireOp",EDGE,"E17.3.0");var subQ2=makeQuery(id+"F4.imprint","INTERSECT",VERTEX,{"derivedFrom":[subQ1,subQ0]});Q5=makeQuery(id+"F4.imprint","IMPRINT",FACE,{"disambiguationData":[TD([[makeQuery(id+"F4.imprint","IMPRINT",EDGE,{"disambiguationData":[TD([[subQ2,-1.0]])],"derivedFrom":subQ1}),1.0]])]});}
            extrude(context, id + "F5", {"entities" : qUnion([Q0, Q1, Q2, Q3, Q4, Q5]), "operationType" : NewBodyOperationType.ADD, "oppositeDirection" : true, "depth" : 2.2 * mm, "offsetDistance" : 25 * mm});
        }
        {
            var Q0;
            Q0=makeQuery(id+"F4.imprint","IMPRINT",FACE,{"disambiguationData":[TD([[makeQuery(id+"F4.imprint","IMPRINT",EDGE,{"derivedFrom":sQuery(id+"F4.wireOp",EDGE,"E17.2.3")}),1.0]])]});
            var Q1;
            Q1=makeQuery(id+"F4.imprint","IMPRINT",FACE,{"disambiguationData":[TD([[makeQuery(id+"F4.imprint","IMPRINT",EDGE,{"derivedFrom":sQuery(id+"F4.wireOp",EDGE,"E17.1.3")}),1.0]])]});
            var Q2;
            Q2=makeQuery(id+"F4.imprint","IMPRINT",FACE,{"disambiguationData":[TD([[makeQuery(id+"F4.imprint","IMPRINT",EDGE,{"derivedFrom":sQuery(id+"F4.wireOp",EDGE,"E16.MirrorC")}),1.0]])]});
            var Q3;
            Q3=makeQuery(id+"F4.imprint","IMPRINT",FACE,{"disambiguationData":[TD([[makeQuery(id+"F4.imprint","IMPRINT",EDGE,{"derivedFrom":sQuery(id+"F4.wireOp",EDGE,"E17.5.3")}),1.0]])]});
            var Q4;
            Q4=makeQuery(id+"F4.imprint","IMPRINT",FACE,{"disambiguationData":[TD([[makeQuery(id+"F4.imprint","IMPRINT",EDGE,{"derivedFrom":sQuery(id+"F4.wireOp",EDGE,"E17.4.3")}),1.0]])]});
            var Q5;
            Q5=makeQuery(id+"F4.imprint","IMPRINT",FACE,{"disambiguationData":[TD([[makeQuery(id+"F4.imprint","IMPRINT",EDGE,{"derivedFrom":sQuery(id+"F4.wireOp",EDGE,"E17.3.3")}),1.0]])]});
            extrude(context, id + "F6", {"entities" : qUnion([Q0, Q1, Q2, Q3, Q4, Q5]), "operationType" : NewBodyOperationType.ADD, "oppositeDirection" : true, "depth" : 2 * mm, "offsetDistance" : 25 * mm});
        }
        {
            var Q0;
            {var subQ0=sQuery(id+"F0.wireOp",EDGE,"E8.3.2");var subQ1=sQuery(id+"F0.wireOp",EDGE,"E8.2.2");Q0=makeQuery(id+"F1.opExtrude","SWEPT_EDGE",EDGE,{"disambiguationData":[OSD([subQ1,subQ0]),TDD([makeQuery(id+"F0.imprint","INTERSECT",VERTEX,{"disambiguationData":[OD(0.0)],"derivedFrom":[subQ1,subQ0]})])]});}
            var Q1;
            {var subQ0=sQuery(id+"F0.wireOp",EDGE,"E8.4.2");var subQ1=sQuery(id+"F0.wireOp",EDGE,"E8.3.2");Q1=makeQuery(id+"F1.opExtrude","SWEPT_EDGE",EDGE,{"disambiguationData":[OSD([subQ1,subQ0]),TDD([makeQuery(id+"F0.imprint","INTERSECT",VERTEX,{"disambiguationData":[OD(0.0)],"derivedFrom":[subQ1,subQ0]})])]});}
            var Q2;
            {var subQ0=sQuery(id+"F0.wireOp",EDGE,"E8.5.2");var subQ1=sQuery(id+"F0.wireOp",EDGE,"E8.4.2");Q2=makeQuery(id+"F1.opExtrude","SWEPT_EDGE",EDGE,{"disambiguationData":[OSD([subQ1,subQ0]),TDD([makeQuery(id+"F0.imprint","INTERSECT",VERTEX,{"disambiguationData":[OD(0.0)],"derivedFrom":[subQ1,subQ0]})])]});}
            var Q3;
            {var subQ0=sQuery(id+"F0.wireOp",EDGE,"E8.5.2");var subQ1=sQuery(id+"F0.wireOp",EDGE,"E3");Q3=makeQuery(id+"F1.opExtrude","SWEPT_EDGE",EDGE,{"disambiguationData":[OSD([subQ1,subQ0]),TDD([makeQuery(id+"F0.imprint","INTERSECT",VERTEX,{"disambiguationData":[OD(0.0)],"derivedFrom":[subQ1,subQ0]})])]});}
            var Q4;
            {var subQ0=sQuery(id+"F0.wireOp",EDGE,"E8.1.2");var subQ1=sQuery(id+"F0.wireOp",EDGE,"E3");Q4=makeQuery(id+"F1.opExtrude","SWEPT_EDGE",EDGE,{"disambiguationData":[OSD([subQ1,subQ0]),TDD([makeQuery(id+"F0.imprint","INTERSECT",VERTEX,{"disambiguationData":[OD(0.0)],"derivedFrom":[subQ1,subQ0]})])]});}
            var Q5;
            {var subQ0=sQuery(id+"F0.wireOp",EDGE,"E8.2.2");var subQ1=sQuery(id+"F0.wireOp",EDGE,"E8.1.2");Q5=makeQuery(id+"F1.opExtrude","SWEPT_EDGE",EDGE,{"disambiguationData":[OSD([subQ1,subQ0]),TDD([makeQuery(id+"F0.imprint","INTERSECT",VERTEX,{"disambiguationData":[OD(0.0)],"derivedFrom":[subQ1,subQ0]})])]});}
            fillet(context, id + "F7", {"entities" : qUnion([Q0, Q1, Q2, Q3, Q4, Q5]), "radius" : 7 * mm, "tangentPropagation" : true, "allowEdgeOverflow" : false});
        }
        {
            var Q0;
            {var subQ0=sQuery(id+"F0.wireOp",EDGE,"E8.2.2");Q0=makeQuery(id+"F5.boolean.opBoolean","MERGE",EDGE,{"derivedFrom":[makeQuery(id+"F1.opExtrude","CAP_EDGE",EDGE,{"disambiguationData":[OSD([subQ0]),TDD([makeQuery(id+"F0.imprint","IMPRINT",EDGE,{"disambiguationData":[TD([[makeQuery(id+"F0.imprint","INTERSECT",VERTEX,{"derivedFrom":[subQ0,sQuery(id+"F0.wireOp",EDGE,"E8.2.4")]}),-1.0]])],"derivedFrom":subQ0})])],"isStart":false}),makeQuery(id+"F1.opExtrude","CAP_EDGE",EDGE,{"disambiguationData":[OSD([subQ0]),TDD([makeQuery(id+"F0.imprint","IMPRINT",EDGE,{"disambiguationData":[TD([[makeQuery(id+"F0.imprint","INTERSECT",VERTEX,{"derivedFrom":[sQuery(id+"F0.wireOp",EDGE,"E8.2.0"),subQ0]}),1.0]])],"derivedFrom":subQ0})])],"isStart":false}),makeQuery(id+"F5.opExtrude","CAP_EDGE",EDGE,{"disambiguationData":[OSD([sQuery(id+"F4.wireOp",EDGE,"E17.2.2")])],"isStart":true})]});}
            var Q1;
            {var subQ0=sQuery(id+"F0.wireOp",EDGE,"E8.1.2");Q1=makeQuery(id+"F2.boolean.opBoolean","MERGE",EDGE,{"derivedFrom":[makeQuery(id+"F1.opExtrude","CAP_EDGE",EDGE,{"disambiguationData":[OSD([subQ0]),TDD([makeQuery(id+"F0.imprint","IMPRINT",EDGE,{"disambiguationData":[TD([[makeQuery(id+"F0.imprint","INTERSECT",VERTEX,{"derivedFrom":[subQ0,sQuery(id+"F0.wireOp",EDGE,"E8.1.4")]}),-1.0]])],"derivedFrom":subQ0})])],"isStart":true}),makeQuery(id+"F1.opExtrude","CAP_EDGE",EDGE,{"disambiguationData":[OSD([subQ0]),TDD([makeQuery(id+"F0.imprint","IMPRINT",EDGE,{"disambiguationData":[TD([[makeQuery(id+"F0.imprint","INTERSECT",VERTEX,{"derivedFrom":[sQuery(id+"F0.wireOp",EDGE,"E8.1.0"),subQ0]}),1.0]])],"derivedFrom":subQ0})])],"isStart":true}),makeQuery(id+"F2.opExtrude","CAP_EDGE",EDGE,{"disambiguationData":[OSD([subQ0])],"isStart":true})]});}
            fillet(context, id + "F8", {"entities" : qUnion([Q0, Q1]), "radius" : 3.5 * mm, "tangentPropagation" : true, "allowEdgeOverflow" : false});
        }
    });
